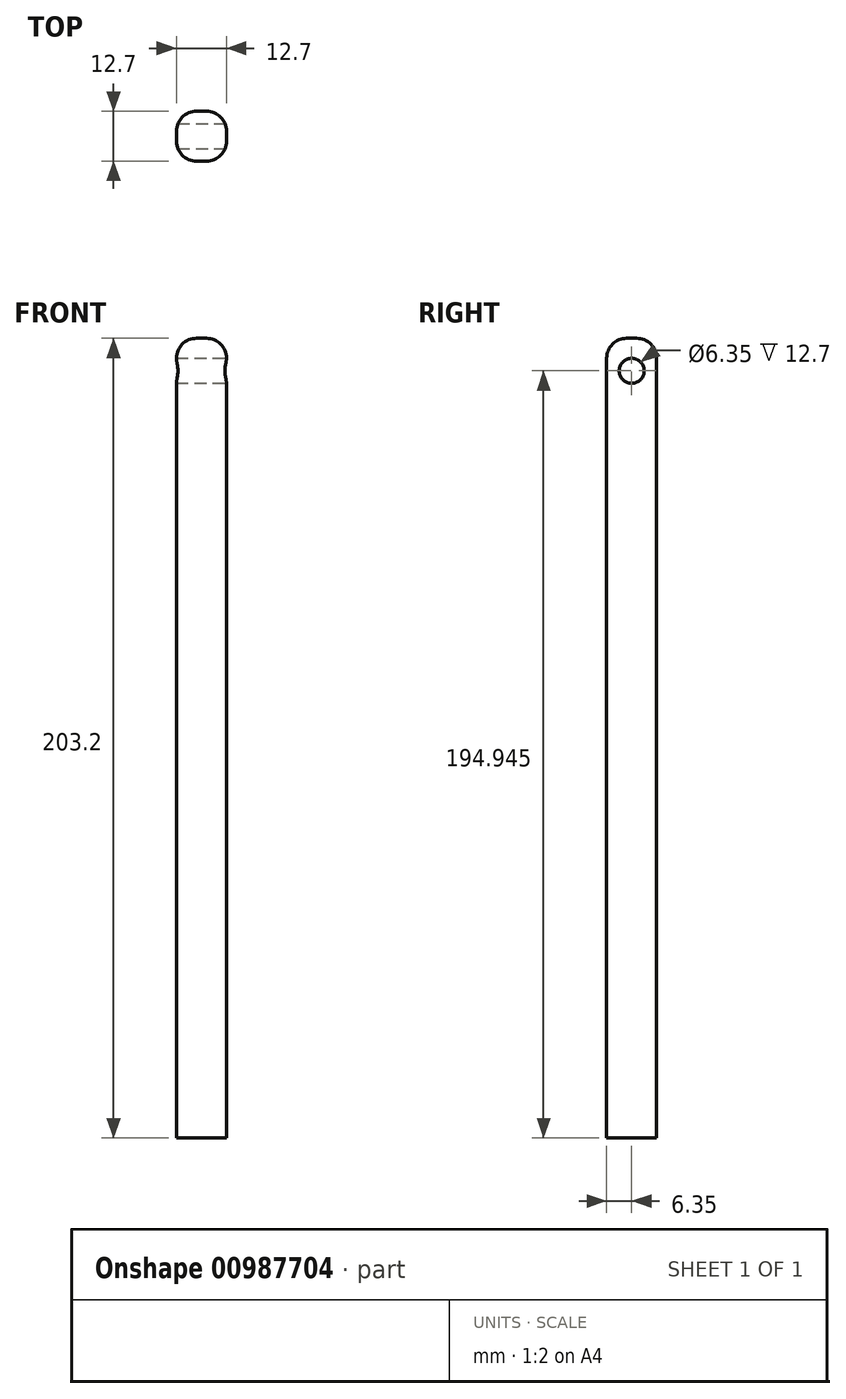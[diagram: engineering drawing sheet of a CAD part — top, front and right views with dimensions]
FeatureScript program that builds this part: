
annotation { "Feature Type Name" : "Feature", "Feature Type Description" : "" }
export const myFeature = defineFeature(function(context is Context, id is Id, definition is map)
    precondition{}
    {
        {
            var Q0;
            Q0=qCreatedBy(makeId("Top.planeOp"),FACE);
            var sketch = newSketch(context, id + "F0", { "sketchPlane" : qUnion([Q0])});
            skLineSegment(sketch, "E0.bottom", {"start": v(-6.35, 6.35) * mm, "end": v(6.35, 6.35) * mm});
            skLineSegment(sketch, "E0.top", {"start": v(-6.35, -6.35) * mm, "end": v(6.35, -6.35) * mm});
            skLineSegment(sketch, "E0.left", {"start": v(-6.35, 6.35) * mm, "end": v(-6.35, -6.35) * mm});
            skLineSegment(sketch, "E0.right", {"start": v(6.35, 6.35) * mm, "end": v(6.35, -6.35) * mm});
            skPoint(sketch, "E0.middle", {"position": v(0, 0) * mm});
            skSolve(sketch);
        }
        {
            var Q0;
            Q0=makeQuery(id+"F0.imprint","IMPRINT",FACE,{"disambiguationData":[TD([[makeQuery(id+"F0.imprint","IMPRINT",EDGE,{"derivedFrom":sQuery(id+"F0.wireOp",EDGE,"E0.bottom")}),-1.0]])]});
            extrude(context, id + "F1", {"entities" : qUnion([Q0]), "depth" : 203.2 * mm, "offsetDistance" : 25.4 * mm});
        }
        {
            var Q0;
            Q0=makeQuery(id+"F1.opExtrude","SWEPT_FACE",FACE,{"disambiguationData":[OSD([sQuery(id+"F0.wireOp",EDGE,"E0.right")])]});
            var sketch = newSketch(context, id + "F2", { "sketchPlane" : qUnion([Q0])});
            skCircle(sketch, "E1", {"center": v(0, 194.94) * mm, "radius": 3.18 * mm});
            skSolve(sketch);
        }
        {
            var Q0;
            Q0=makeQuery(id+"F2.imprint","IMPRINT",FACE,{"disambiguationData":[TD([[makeQuery(id+"F2.imprint","IMPRINT",EDGE,{"derivedFrom":sQuery(id+"F2.wireOp",EDGE,"E1")}),1.0]])]});
            extrude(context, id + "F3", {"entities" : qUnion([Q0]), "operationType" : NewBodyOperationType.REMOVE, "oppositeDirection" : true, "depth" : 25.4 * mm, "offsetDistance" : 25.4 * mm});
        }
        {
            var Q0;
            Q0=makeQuery(id+"F1.opExtrude","SWEPT_EDGE",EDGE,{"disambiguationData":[OSD([sQuery(id+"F0.wireOp",EDGE,"E0.bottom"),sQuery(id+"F0.wireOp",EDGE,"E0.right")])]});
            var Q1;
            Q1=makeQuery(id+"F1.opExtrude","SWEPT_EDGE",EDGE,{"disambiguationData":[OSD([sQuery(id+"F0.wireOp",EDGE,"E0.top"),sQuery(id+"F0.wireOp",EDGE,"E0.right")])]});
            var Q2;
            Q2=makeQuery(id+"F1.opExtrude","SWEPT_EDGE",EDGE,{"disambiguationData":[OSD([sQuery(id+"F0.wireOp",EDGE,"E0.bottom"),sQuery(id+"F0.wireOp",EDGE,"E0.left")])]});
            var Q3;
            Q3=makeQuery(id+"F1.opExtrude","SWEPT_EDGE",EDGE,{"disambiguationData":[OSD([sQuery(id+"F0.wireOp",EDGE,"E0.top"),sQuery(id+"F0.wireOp",EDGE,"E0.left")])]});
            var Q4;
            Q4=makeQuery(id+"F1.opExtrude","CAP_EDGE",EDGE,{"disambiguationData":[OSD([sQuery(id+"F0.wireOp",EDGE,"E0.bottom")])],"isStart":false});
            var Q5;
            Q5=makeQuery(id+"F1.opExtrude","CAP_EDGE",EDGE,{"disambiguationData":[OSD([sQuery(id+"F0.wireOp",EDGE,"E0.top")])],"isStart":false});
            var Q6;
            Q6=makeQuery(id+"F1.opExtrude","CAP_EDGE",EDGE,{"disambiguationData":[OSD([sQuery(id+"F0.wireOp",EDGE,"E0.right")])],"isStart":false});
            var Q7;
            Q7=makeQuery(id+"F1.opExtrude","CAP_EDGE",EDGE,{"disambiguationData":[OSD([sQuery(id+"F0.wireOp",EDGE,"E0.left")])],"isStart":false});
            fillet(context, id + "F4", {"entities" : qUnion([Q0, Q1, Q2, Q3, Q4, Q5, Q6, Q7]), "radius" : 5.08 * mm, "tangentPropagation" : true, "allowEdgeOverflow" : false});
        }
    });
